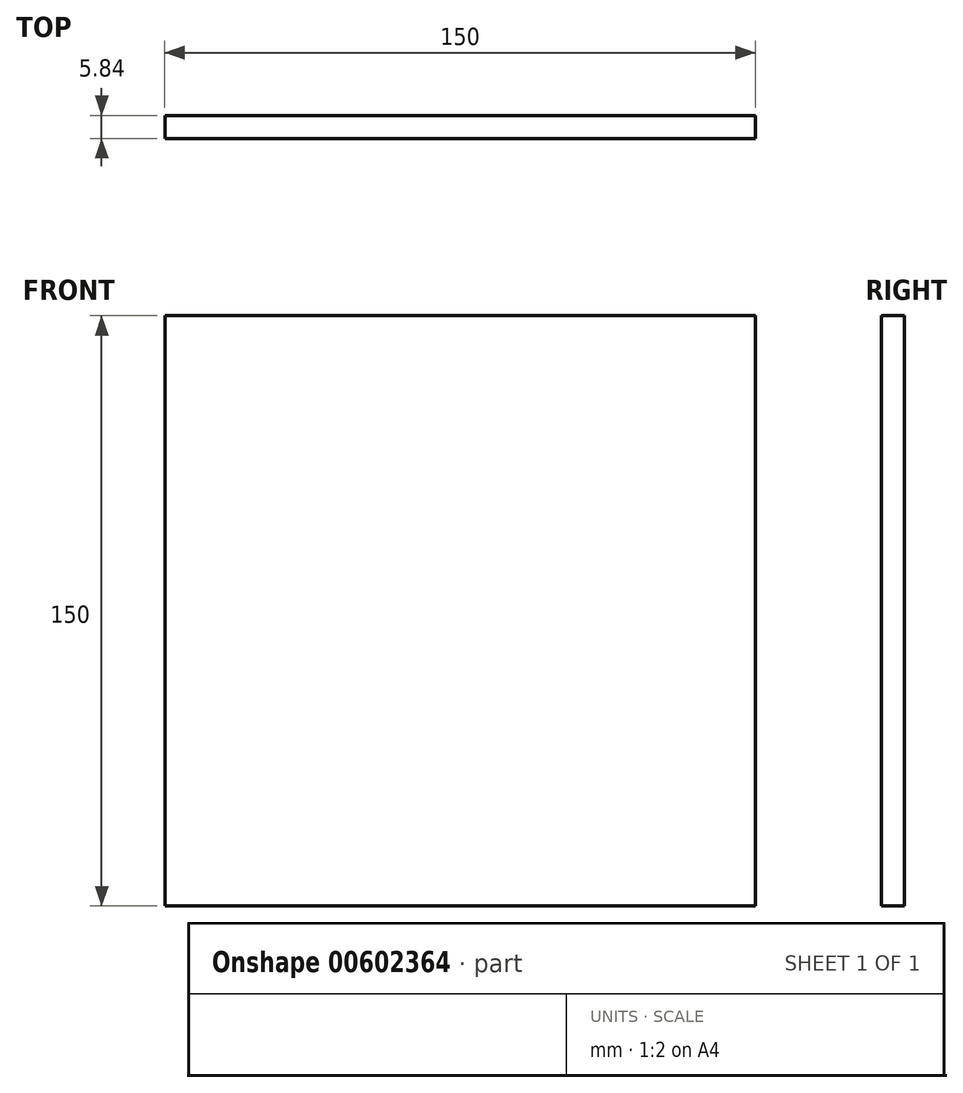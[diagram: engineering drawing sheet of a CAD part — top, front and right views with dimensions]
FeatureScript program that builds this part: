
annotation { "Feature Type Name" : "Feature", "Feature Type Description" : "" }
export const myFeature = defineFeature(function(context is Context, id is Id, definition is map)
    precondition{}
    {
        {
            var Q0;
            Q0=qCreatedBy(makeId("Front.planeOp"),FACE);
            var sketch = newSketch(context, id + "F0", { "sketchPlane" : qUnion([Q0])});
            skLineSegment(sketch, "E0", {"start": v(-77.26, 126.3) * mm, "end": v(72.74, 126.3) * mm});
            skLineSegment(sketch, "E1", {"start": v(72.74, 126.3) * mm, "end": v(72.74, -23.7) * mm});
            skLineSegment(sketch, "E2", {"start": v(72.74, -23.7) * mm, "end": v(-77.26, -23.7) * mm});
            skLineSegment(sketch, "E3", {"start": v(-77.26, -23.7) * mm, "end": v(-77.26, 126.3) * mm});
            skSolve(sketch);
        }
        {
            var Q0;
            Q0 = qSketchRegion(id + "F0", true);
            extrude(context, id + "F1", {"entities" : qUnion([Q0]), "depth" : 5.84 * mm, "offsetDistance" : 25.4 * mm});
        }
    });
